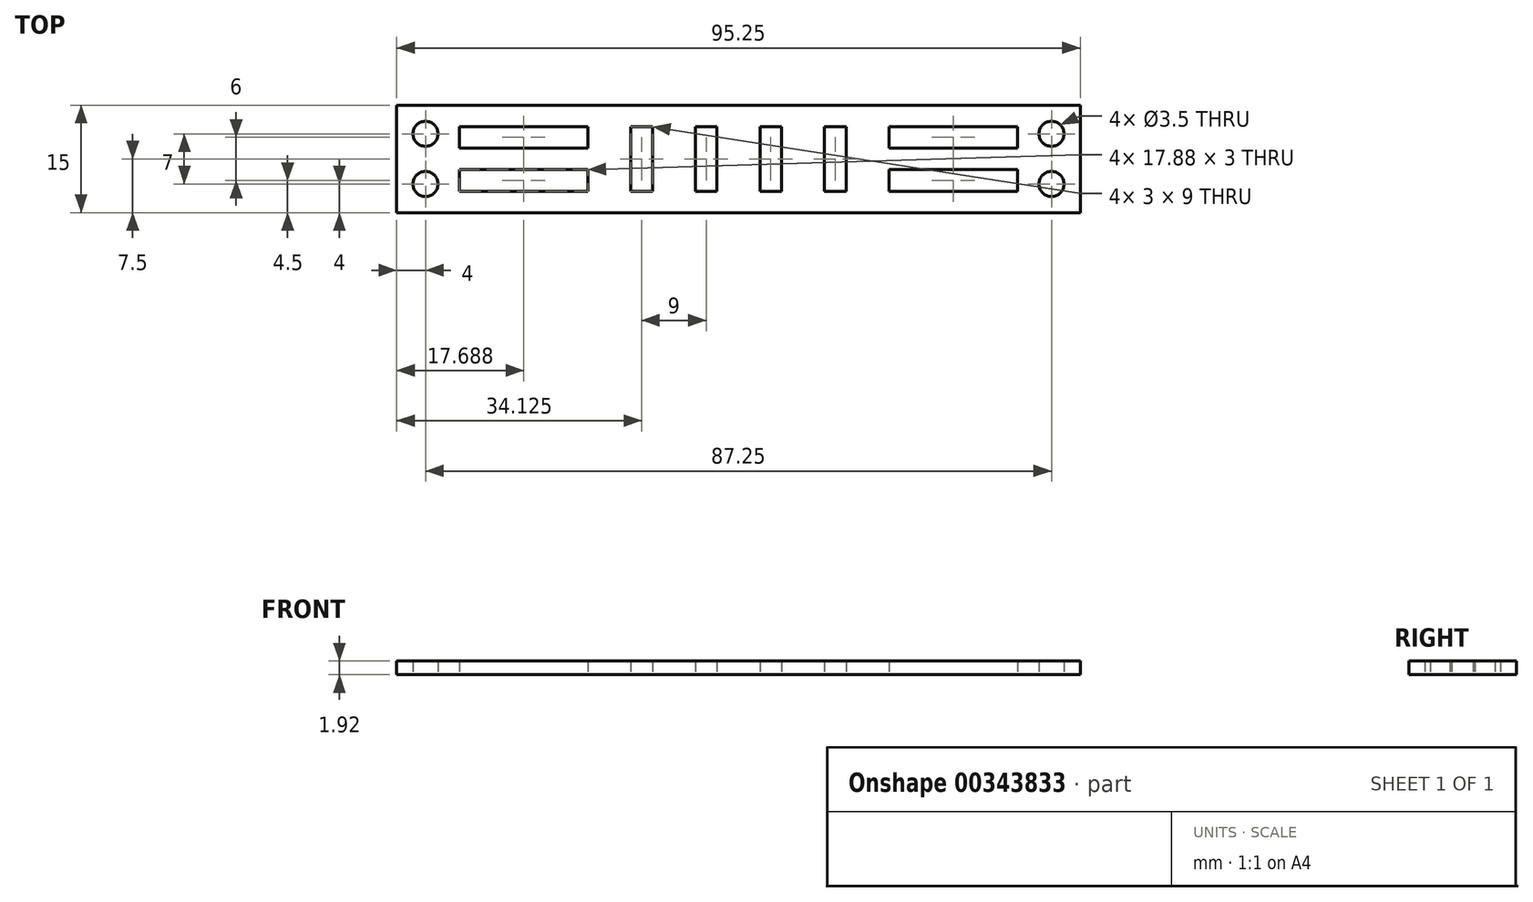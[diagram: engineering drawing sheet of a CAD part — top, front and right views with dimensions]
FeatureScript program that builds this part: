
annotation { "Feature Type Name" : "Feature", "Feature Type Description" : "" }
export const myFeature = defineFeature(function(context is Context, id is Id, definition is map)
    precondition{}
    {
        {
            var Q0;
            Q0=qCreatedBy(makeId("Top.planeOp"),FACE);
            var sketch = newSketch(context, id + "F0", { "sketchPlane" : qUnion([Q0])});
            skLineSegment(sketch, "E0.bottom", {"start": v(0, 0) * mm, "end": v(95.25, 0) * mm});
            skLineSegment(sketch, "E0.top", {"start": v(0, 15) * mm, "end": v(95.25, 15) * mm});
            skLineSegment(sketch, "E0.left", {"start": v(0, 0) * mm, "end": v(0, 15) * mm});
            skLineSegment(sketch, "E0.right", {"start": v(95.25, 0) * mm, "end": v(95.25, 15) * mm});
            skCircle(sketch, "E1", {"center": v(4, 11) * mm, "radius": 1.75 * mm});
            skCircle(sketch, "E2", {"center": v(4, 4) * mm, "radius": 1.75 * mm});
            skLineSegment(sketch, "E3", {"start": v(47.63, 15) * mm, "end": v(47.63, 0) * mm, "construction": true});
            skLineSegment(sketch, "E4.bottom", {"start": v(8.75, 12) * mm, "end": v(26.62, 12) * mm});
            skLineSegment(sketch, "E4.top", {"start": v(8.75, 9) * mm, "end": v(26.62, 9) * mm});
            skLineSegment(sketch, "E4.left", {"start": v(8.75, 12) * mm, "end": v(8.75, 9) * mm});
            skLineSegment(sketch, "E4.right", {"start": v(26.62, 12) * mm, "end": v(26.62, 9) * mm});
            skLineSegment(sketch, "E5.bottom", {"start": v(8.75, 6) * mm, "end": v(26.62, 6) * mm});
            skLineSegment(sketch, "E5.top", {"start": v(8.75, 3) * mm, "end": v(26.62, 3) * mm});
            skLineSegment(sketch, "E5.left", {"start": v(8.75, 6) * mm, "end": v(8.75, 3) * mm});
            skLineSegment(sketch, "E5.right", {"start": v(26.62, 6) * mm, "end": v(26.62, 3) * mm});
            skLineSegment(sketch, "E6.bottom", {"start": v(32.62, 12) * mm, "end": v(35.62, 12) * mm});
            skLineSegment(sketch, "E6.top", {"start": v(32.62, 3) * mm, "end": v(35.62, 3) * mm});
            skLineSegment(sketch, "E6.left", {"start": v(32.62, 12) * mm, "end": v(32.62, 3) * mm});
            skLineSegment(sketch, "E6.right", {"start": v(35.62, 12) * mm, "end": v(35.62, 3) * mm});
            skPoint(sketch, "E7.firstSnap0", {"position": v(34.12, 12) * mm});
            skLineSegment(sketch, "E7.bottom", {"start": v(41.62, 12) * mm, "end": v(44.63, 12) * mm});
            skLineSegment(sketch, "E7.top", {"start": v(41.62, 3) * mm, "end": v(44.63, 3) * mm});
            skLineSegment(sketch, "E7.left", {"start": v(41.62, 12) * mm, "end": v(41.62, 3) * mm});
            skLineSegment(sketch, "E7.right", {"start": v(44.63, 12) * mm, "end": v(44.63, 3) * mm});
            skLineSegment(sketch, "E8.MirrorCS", {"start": v(62.63, 12) * mm, "end": v(59.63, 12) * mm});
            skPoint(sketch, "E9.MirrorP", {"position": v(61.13, 12) * mm});
            skLineSegment(sketch, "E10.MirrorCS", {"start": v(53.63, 12) * mm, "end": v(53.63, 3) * mm});
            skLineSegment(sketch, "E11.MirrorCS", {"start": v(53.63, 12) * mm, "end": v(50.63, 12) * mm});
            skLineSegment(sketch, "E12.MirrorCS", {"start": v(62.63, 3) * mm, "end": v(59.63, 3) * mm});
            skLineSegment(sketch, "E13.MirrorCS", {"start": v(59.63, 12) * mm, "end": v(59.63, 3) * mm});
            skLineSegment(sketch, "E14.MirrorCS", {"start": v(53.63, 3) * mm, "end": v(50.63, 3) * mm});
            skLineSegment(sketch, "E15.MirrorCS", {"start": v(50.63, 12) * mm, "end": v(50.63, 3) * mm});
            skLineSegment(sketch, "E16.MirrorCS", {"start": v(86.5, 3) * mm, "end": v(68.63, 3) * mm});
            skLineSegment(sketch, "E17.MirrorCS", {"start": v(86.5, 9) * mm, "end": v(68.63, 9) * mm});
            skLineSegment(sketch, "E18.MirrorCS", {"start": v(86.5, 6) * mm, "end": v(86.5, 3) * mm});
            skLineSegment(sketch, "E19.MirrorCS", {"start": v(86.5, 12) * mm, "end": v(86.5, 9) * mm});
            skLineSegment(sketch, "E20.MirrorCS", {"start": v(62.63, 12) * mm, "end": v(62.63, 3) * mm});
            skLineSegment(sketch, "E21.MirrorCS", {"start": v(68.63, 12) * mm, "end": v(68.63, 9) * mm});
            skLineSegment(sketch, "E22.MirrorCS", {"start": v(68.63, 6) * mm, "end": v(68.63, 3) * mm});
            skLineSegment(sketch, "E23.MirrorCS", {"start": v(86.5, 6) * mm, "end": v(68.63, 6) * mm});
            skLineSegment(sketch, "E24.MirrorCS", {"start": v(86.5, 12) * mm, "end": v(68.63, 12) * mm});
            skCircle(sketch, "E25.MirrorC", {"center": v(91.25, 4) * mm, "radius": 1.75 * mm});
            skCircle(sketch, "E26.MirrorC", {"center": v(91.25, 11) * mm, "radius": 1.75 * mm});
            skSolve(sketch);
        }
        {
            var Q0;
            Q0 = qSketchRegion(id + "F0", true);
            extrude(context, id + "F1", {"entities" : qUnion([Q0]), "depth" : (.32 * 6) * mm});
        }
    });
